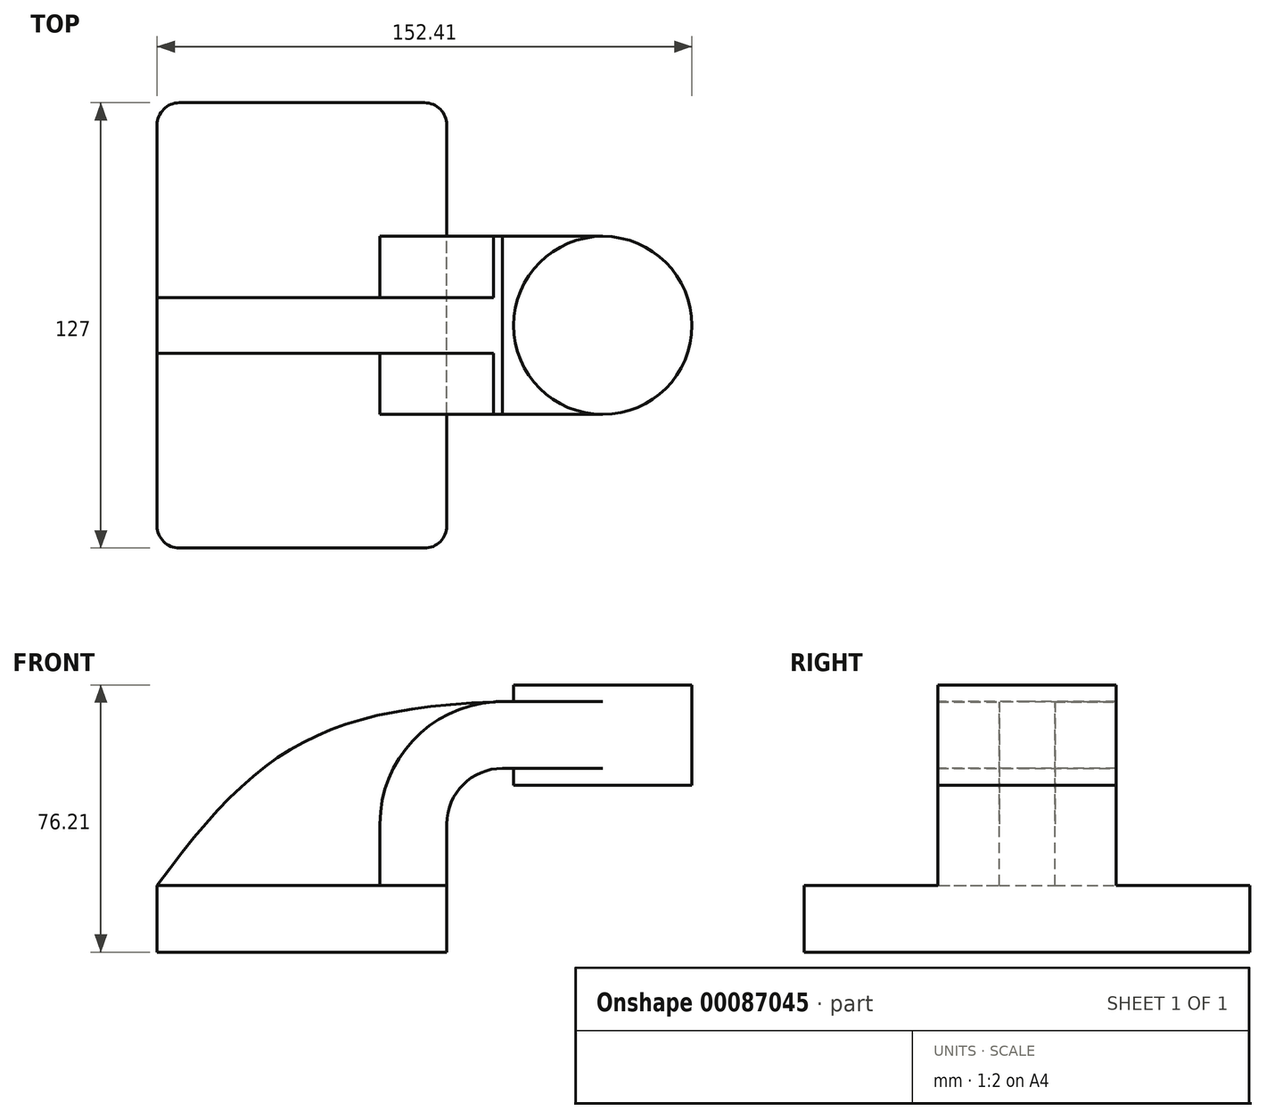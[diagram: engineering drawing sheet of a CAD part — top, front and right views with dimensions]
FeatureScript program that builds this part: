
annotation { "Feature Type Name" : "Feature", "Feature Type Description" : "" }
export const myFeature = defineFeature(function(context is Context, id is Id, definition is map)
    precondition{}
    {
        {
            var Q0;
            Q0=qCreatedBy(makeId("Front.planeOp"),FACE);
            var sketch = newSketch(context, id + "F0", { "sketchPlane" : qUnion([Q0])});
            skLineSegment(sketch, "E0.bottom", {"start": v(41.28, -9.52) * mm, "end": v(-41.27, -9.53) * mm});
            skLineSegment(sketch, "E0.top", {"start": v(41.27, 9.53) * mm, "end": v(-41.28, 9.53) * mm});
            skLineSegment(sketch, "E0.left", {"start": v(41.28, -9.52) * mm, "end": v(41.27, 9.53) * mm});
            skLineSegment(sketch, "E0.right", {"start": v(-41.27, -9.53) * mm, "end": v(-41.28, 9.53) * mm});
            skPoint(sketch, "E0.middle", {"position": v(0, 0) * mm});
            skLineSegment(sketch, "E1.bottom", {"start": v(111.12, 38.1) * mm, "end": v(60.32, 38.1) * mm});
            skLineSegment(sketch, "E1.top", {"start": v(111.12, 66.68) * mm, "end": v(60.32, 66.68) * mm});
            skLineSegment(sketch, "E1.left", {"start": v(111.12, 38.1) * mm, "end": v(111.12, 66.68) * mm});
            skLineSegment(sketch, "E1.right", {"start": v(60.32, 38.1) * mm, "end": v(60.32, 66.68) * mm});
            skPoint(sketch, "E1.middle", {"position": v(85.72, 52.39) * mm});
            skLineSegment(sketch, "E2", {"start": v(41.27, 9.53) * mm, "end": v(41.27, 27) * mm});
            skArc(sketch, "E3", {"start": v(41.27, 27) * mm, "mid": v(45.92, 38.23) * mm, "end": v(57.15, 42.88) * mm});
            skLineSegment(sketch, "E4", {"start": v(57.15, 42.88) * mm, "end": v(85.72, 42.88) * mm});
            skLineSegment(sketch, "E5.0", {"start": v(57.15, 61.93) * mm, "end": v(85.72, 61.93) * mm});
            skArc(sketch, "E5.1", {"start": v(22.22, 27) * mm, "mid": v(32.45, 51.7) * mm, "end": v(57.15, 61.93) * mm});
            skLineSegment(sketch, "E5.2", {"start": v(22.23, 9.53) * mm, "end": v(22.23, 27) * mm});
            skLineSegment(sketch, "E6", {"start": v(85.72, 38.1) * mm, "end": v(85.72, 66.68) * mm});
            skFitSpline(sketch, "E7", {"points": [v(-41.28, 9.53) * mm, v(57.15, 61.93) * mm], "startDerivative": vector(85.1, 116.47) * mm, "endDerivative": vector(154.87, 5.04) * mm});
            skSolve(sketch);
        }
        {
            var Q0;
            Q0=makeQuery(id+"F0.imprint","IMPRINT",FACE,{"disambiguationData":[TD([[makeQuery(id+"F0.imprint","IMPRINT",EDGE,{"derivedFrom":sQuery(id+"F0.wireOp",EDGE,"E0.bottom")}),-1.0]])]});
            extrude(context, id + "F1", {"entities" : qUnion([Q0]), "endBound" : BoundingType.SYMMETRIC, "depth" : 127 * mm});
        }
        {
            var Q0;
            {var subQ0=sQuery(id+"F0.wireOp",EDGE,"E4");var subQ1=sQuery(id+"F0.wireOp",EDGE,"E1.right");var subQ2=makeQuery(id+"F0.imprint","INTERSECT",VERTEX,{"derivedFrom":[subQ1,subQ0]});Q0=makeQuery(id+"F0.imprint","IMPRINT",FACE,{"disambiguationData":[TD([[makeQuery(id+"F0.imprint","IMPRINT",EDGE,{"disambiguationData":[TD([[subQ2,-1.0]])],"derivedFrom":subQ1}),-1.0]])]});}
            var Q1;
            {var subQ1=sQuery(id+"F0.wireOp",EDGE,"E2");Q1=makeQuery(id+"F0.imprint","IMPRINT",FACE,{"disambiguationData":[TD([[makeQuery(id+"F0.imprint","IMPRINT",EDGE,{"derivedFrom":subQ1}),1.0]])]});}
            extrude(context, id + "F2", {"entities" : qUnion([Q0, Q1]), "operationType" : NewBodyOperationType.ADD, "endBound" : BoundingType.SYMMETRIC, "depth" : 50.8 * mm});
        }
        {
            var Q0;
            {var subQ3=sQuery(id+"F0.wireOp",EDGE,"E5.2");Q0=makeQuery(id+"F0.imprint","IMPRINT",FACE,{"disambiguationData":[TD([[makeQuery(id+"F0.imprint","IMPRINT",EDGE,{"derivedFrom":subQ3}),1.0]])]});}
            extrude(context, id + "F3", {"entities" : qUnion([Q0]), "operationType" : NewBodyOperationType.ADD, "endBound" : BoundingType.SYMMETRIC, "depth" : 15.88 * mm});
        }
        {
            var Q0;
            {var subQ0=sQuery(id+"F0.wireOp",EDGE,"E1.left");Q0=makeQuery(id+"F0.imprint","IMPRINT",FACE,{"disambiguationData":[TD([[makeQuery(id+"F0.imprint","IMPRINT",EDGE,{"derivedFrom":subQ0}),1.0]])]});}
            var Q1;
            Q1=sQuery(id+"F0.wireOp",EDGE,"E6");
            revolve(context, id + "F4", {"operationType" : NewBodyOperationType.ADD, "entities" : qUnion([Q0]), "axis" : qUnion([Q1]), "revolveType" : RevolveType.FULL});
        }
        {
            var Q0;
            Q0=makeQuery(id+"F1.opExtrude","CAP_EDGE",EDGE,{"disambiguationData":[OSD([sQuery(id+"F0.wireOp",EDGE,"E0.right")])],"isStart":false});
            var Q1;
            Q1=makeQuery(id+"F1.opExtrude","CAP_EDGE",EDGE,{"disambiguationData":[OSD([sQuery(id+"F0.wireOp",EDGE,"E0.left")])],"isStart":false});
            var Q2;
            Q2=makeQuery(id+"F1.opExtrude","CAP_EDGE",EDGE,{"disambiguationData":[OSD([sQuery(id+"F0.wireOp",EDGE,"E0.left")])],"isStart":true});
            var Q3;
            Q3=makeQuery(id+"F1.opExtrude","CAP_EDGE",EDGE,{"disambiguationData":[OSD([sQuery(id+"F0.wireOp",EDGE,"E0.right")])],"isStart":true});
            fillet(context, id + "F5", {"entities" : qUnion([Q0, Q1, Q2, Q3]), "radius" : 6.35 * mm, "tangentPropagation" : true, "allowEdgeOverflow" : false});
        }
    });
